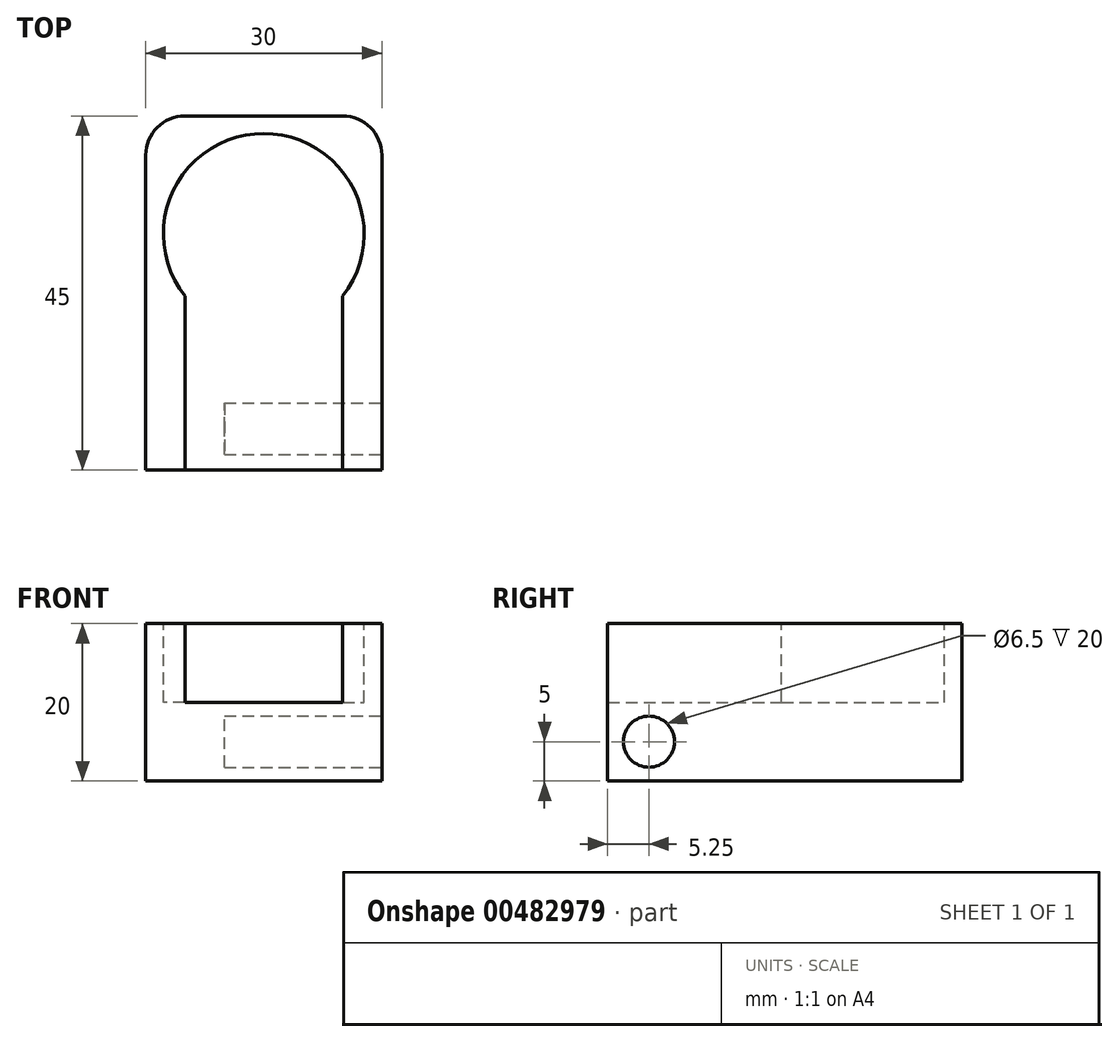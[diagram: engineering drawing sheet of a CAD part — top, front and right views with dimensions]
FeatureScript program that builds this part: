
annotation { "Feature Type Name" : "Feature", "Feature Type Description" : "" }
export const myFeature = defineFeature(function(context is Context, id is Id, definition is map)
    precondition{}
    {
        {
            var Q0;
            Q0=qCreatedBy(makeId("Top.planeOp"),FACE);
            var sketch = newSketch(context, id + "F0", { "sketchPlane" : qUnion([Q0])});
            skLineSegment(sketch, "E0.bottom", {"start": v(0, 0) * mm, "end": v(30, 0) * mm});
            skLineSegment(sketch, "E0.top", {"start": v(0, 45) * mm, "end": v(30, 45) * mm});
            skLineSegment(sketch, "E0.left", {"start": v(0, 0) * mm, "end": v(0, 45) * mm});
            skLineSegment(sketch, "E0.right", {"start": v(30, 0) * mm, "end": v(30, 45) * mm});
            skSolve(sketch);
        }
        {
            var Q0;
            Q0=makeQuery(id+"F0.imprint","IMPRINT",FACE,{"disambiguationData":[TD([[makeQuery(id+"F0.imprint","IMPRINT",EDGE,{"derivedFrom":sQuery(id+"F0.wireOp",EDGE,"E0.bottom")}),1.0]])]});
            extrude(context, id + "F1", {"entities" : qUnion([Q0]), "depth" : 20 * mm});
        }
        {
            var Q0;
            Q0=makeQuery(id+"F1.opExtrude","CAP_FACE",FACE,{"disambiguationData":[OSD([sQuery(id+"F0.wireOp",EDGE,"E0.bottom"),sQuery(id+"F0.wireOp",EDGE,"E0.top"),sQuery(id+"F0.wireOp",EDGE,"E0.left"),sQuery(id+"F0.wireOp",EDGE,"E0.right")])],"isStart":false});
            var sketch = newSketch(context, id + "F2", { "sketchPlane" : qUnion([Q0])});
            skCircle(sketch, "E1", {"center": v(15, 30) * mm, "radius": 12.75 * mm});
            skSolve(sketch);
        }
        {
            var Q0;
            Q0=makeQuery(id+"F2.imprint","IMPRINT",FACE,{"disambiguationData":[TD([[makeQuery(id+"F2.imprint","IMPRINT",EDGE,{"derivedFrom":sQuery(id+"F2.wireOp",EDGE,"E1")}),1.0]])]});
            extrude(context, id + "F3", {"entities" : qUnion([Q0]), "operationType" : NewBodyOperationType.REMOVE, "oppositeDirection" : true, "depth" : 10 * mm});
        }
        {
            var Q0;
            Q0=makeQuery(id+"F1.opExtrude","SWEPT_FACE",FACE,{"disambiguationData":[OSD([sQuery(id+"F0.wireOp",EDGE,"E0.right")])]});
            var sketch = newSketch(context, id + "F4", { "sketchPlane" : qUnion([Q0])});
            skCircle(sketch, "E2", {"center": v(5.25, 5) * mm, "radius": 3.25 * mm});
            skSolve(sketch);
        }
        {
            var Q0;
            Q0 = qSketchRegion(id + "F4", true);
            extrude(context, id + "F5", {"entities" : qUnion([Q0]), "operationType" : NewBodyOperationType.REMOVE, "oppositeDirection" : true, "depth" : 20 * mm});
        }
        {
            var Q0;
            Q0=makeQuery(id+"F1.opExtrude","CAP_FACE",FACE,{"disambiguationData":[OSD([sQuery(id+"F0.wireOp",EDGE,"E0.bottom"),sQuery(id+"F0.wireOp",EDGE,"E0.top"),sQuery(id+"F0.wireOp",EDGE,"E0.left"),sQuery(id+"F0.wireOp",EDGE,"E0.right")])],"isStart":false});
            var sketch = newSketch(context, id + "F6", { "sketchPlane" : qUnion([Q0])});
            skLineSegment(sketch, "E3.bottom", {"start": v(5, 0) * mm, "end": v(25, 0) * mm});
            skLineSegment(sketch, "E3.top", {"start": v(5, 22.1) * mm, "end": v(25, 22.1) * mm});
            skLineSegment(sketch, "E3.left", {"start": v(5, 0) * mm, "end": v(5, 22.1) * mm});
            skLineSegment(sketch, "E3.right", {"start": v(25, 0) * mm, "end": v(25, 22.1) * mm});
            skSolve(sketch);
        }
        {
            var Q0;
            Q0=makeQuery(id+"F6.imprint","IMPRINT",FACE,{"disambiguationData":[TD([[makeQuery(id+"F6.imprint","IMPRINT",EDGE,{"derivedFrom":sQuery(id+"F6.wireOp",EDGE,"E3.bottom")}),1.0]])]});
            extrude(context, id + "F7", {"entities" : qUnion([Q0]), "operationType" : NewBodyOperationType.REMOVE, "oppositeDirection" : true, "depth" : 10 * mm});
        }
        {
            var Q0;
            Q0=makeQuery(id+"F1.opExtrude","SWEPT_EDGE",EDGE,{"disambiguationData":[OSD([sQuery(id+"F0.wireOp",EDGE,"E0.top"),sQuery(id+"F0.wireOp",EDGE,"E0.left")])]});
            var Q1;
            Q1=makeQuery(id+"F1.opExtrude","SWEPT_EDGE",EDGE,{"disambiguationData":[OSD([sQuery(id+"F0.wireOp",EDGE,"E0.top"),sQuery(id+"F0.wireOp",EDGE,"E0.right")])]});
            fillet(context, id + "F8", {"entities" : qUnion([Q0, Q1]), "radius" : 5 * mm, "tangentPropagation" : true, "allowEdgeOverflow" : false});
        }
    });
